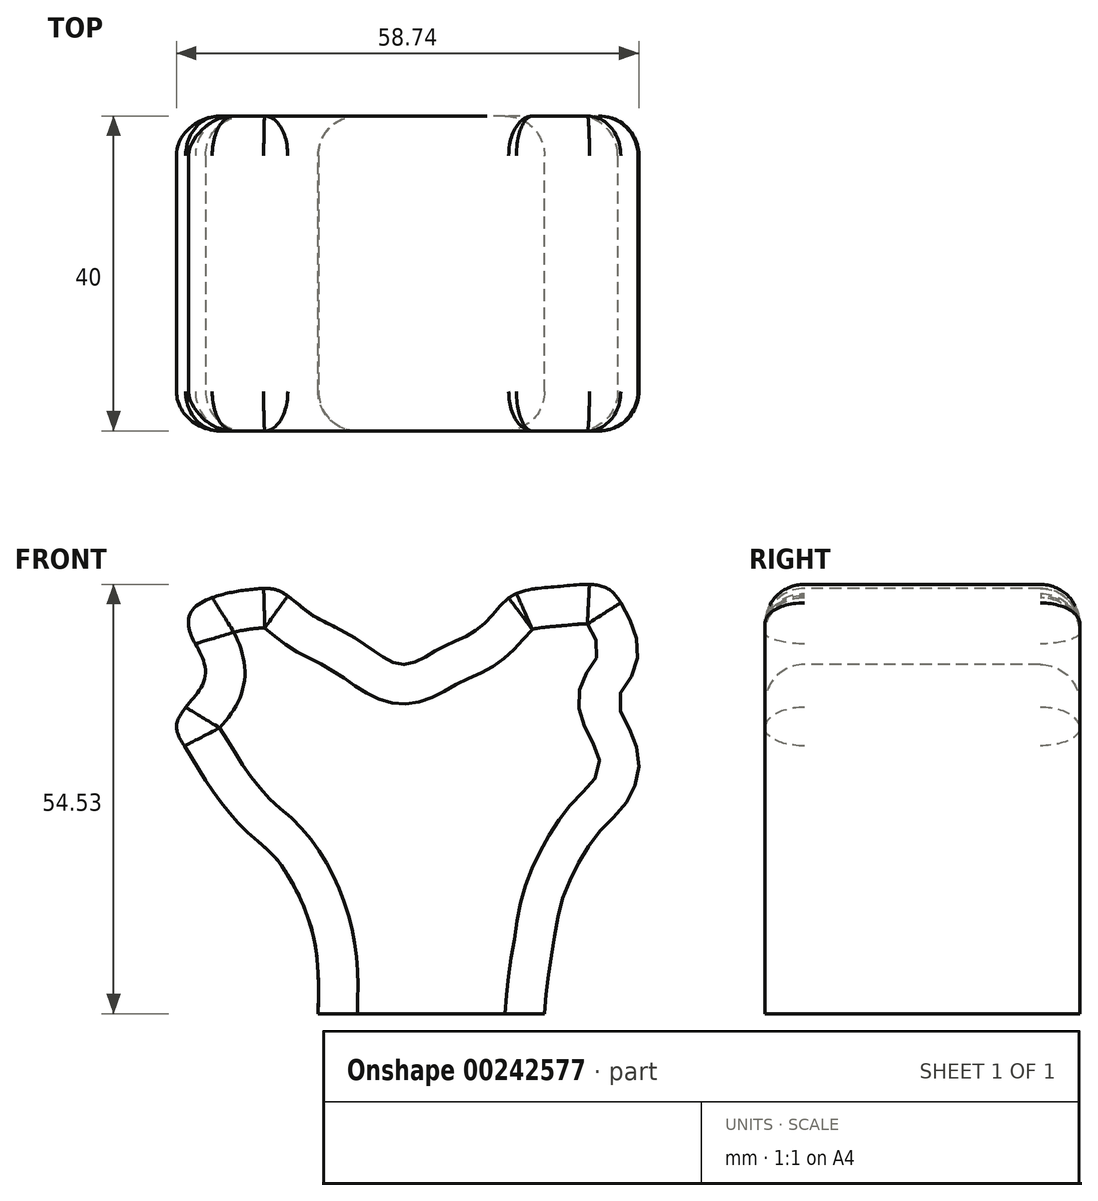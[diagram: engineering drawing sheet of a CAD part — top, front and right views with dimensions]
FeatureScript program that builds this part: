
annotation { "Feature Type Name" : "Feature", "Feature Type Description" : "" }
export const myFeature = defineFeature(function(context is Context, id is Id, definition is map)
    precondition{}
    {
        {
            var Q0;
            Q0=qCreatedBy(makeId("Front.planeOp"),FACE);
            var sketch = newSketch(context, id + "F0", { "sketchPlane" : qUnion([Q0])});
            skFitSpline(sketch, "E0", {"points": [v(-15.58, 0) * mm, v(-15.58, 5.4) * mm, v(-16.78, 11.99) * mm, v(-20.98, 19.78) * mm, v(-24.57, 23.07) * mm, v(-29.07, 28.47) * mm, v(-32.06, 33.26) * mm, v(-33.56, 36.26) * mm, v(-32.36, 38.96) * mm, v(-29.97, 42.55) * mm, v(-30.57, 45.85) * mm, v(-31.76, 48.25) * mm, v(-31.76, 50.94) * mm, v(-28.47, 53.04) * mm, v(-23.67, 53.94) * mm, v(-20.38, 53.64) * mm, v(-16.78, 50.94) * mm, v(-13.48, 49.14) * mm, v(-8.99, 46.45) * mm, v(-4.8, 44.35) * mm, v(0, 46.45) * mm, v(5.1, 49.14) * mm, v(8.99, 53.04) * mm, v(14.68, 54.24) * mm, v(20.68, 54.24) * mm, v(23.07, 51.84) * mm, v(24.87, 47.65) * mm, v(24.87, 44.65) * mm, v(23.67, 41.95) * mm, v(22.47, 39.86) * mm, v(23.37, 37.46) * mm, v(24.57, 34.76) * mm, v(25.17, 31.76) * mm, v(23.67, 26.97) * mm, v(20.38, 23.37) * mm, v(17.38, 18.88) * mm, v(15.28, 14.08) * mm, v(14.38, 9.29) * mm, v(13.48, 3.6) * mm, v(13.19, 0) * mm], "startDerivative": vector(4.9, 187.91) * mm, "endDerivative": vector(-8.22, -144.64) * mm});
            skFitSpline(sketch, "E1", {"points": [v(13.19, 0) * mm, v(-15.58, 0) * mm], "startDerivative": vector(-28.77, 0) * mm, "endDerivative": vector(-28.77, 0) * mm});
            skSolve(sketch);
        }
        {
            var Q0;
            Q0 = qSketchRegion(id + "F0", true);
            extrude(context, id + "F1", {"entities" : qUnion([Q0]), "depth" : 40 * mm});
        }
        {
            var Q0;
            Q0=makeQuery(id+"F1.opExtrude","CAP_EDGE",EDGE,{"disambiguationData":[OSD([sQuery(id+"F0.wireOp",EDGE,"E0")])],"isStart":false});
            fillet(context, id + "F2", {"entities" : qUnion([Q0]), "radius" : 5 * mm, "tangentPropagation" : true, "allowEdgeOverflow" : false});
        }
        {
            var Q0;
            Q0=makeQuery(id+"F1.opExtrude","CAP_EDGE",EDGE,{"disambiguationData":[OSD([sQuery(id+"F0.wireOp",EDGE,"E0")])],"isStart":true});
            fillet(context, id + "F3", {"entities" : qUnion([Q0]), "radius" : 5 * mm, "tangentPropagation" : true, "allowEdgeOverflow" : false});
        }
    });
